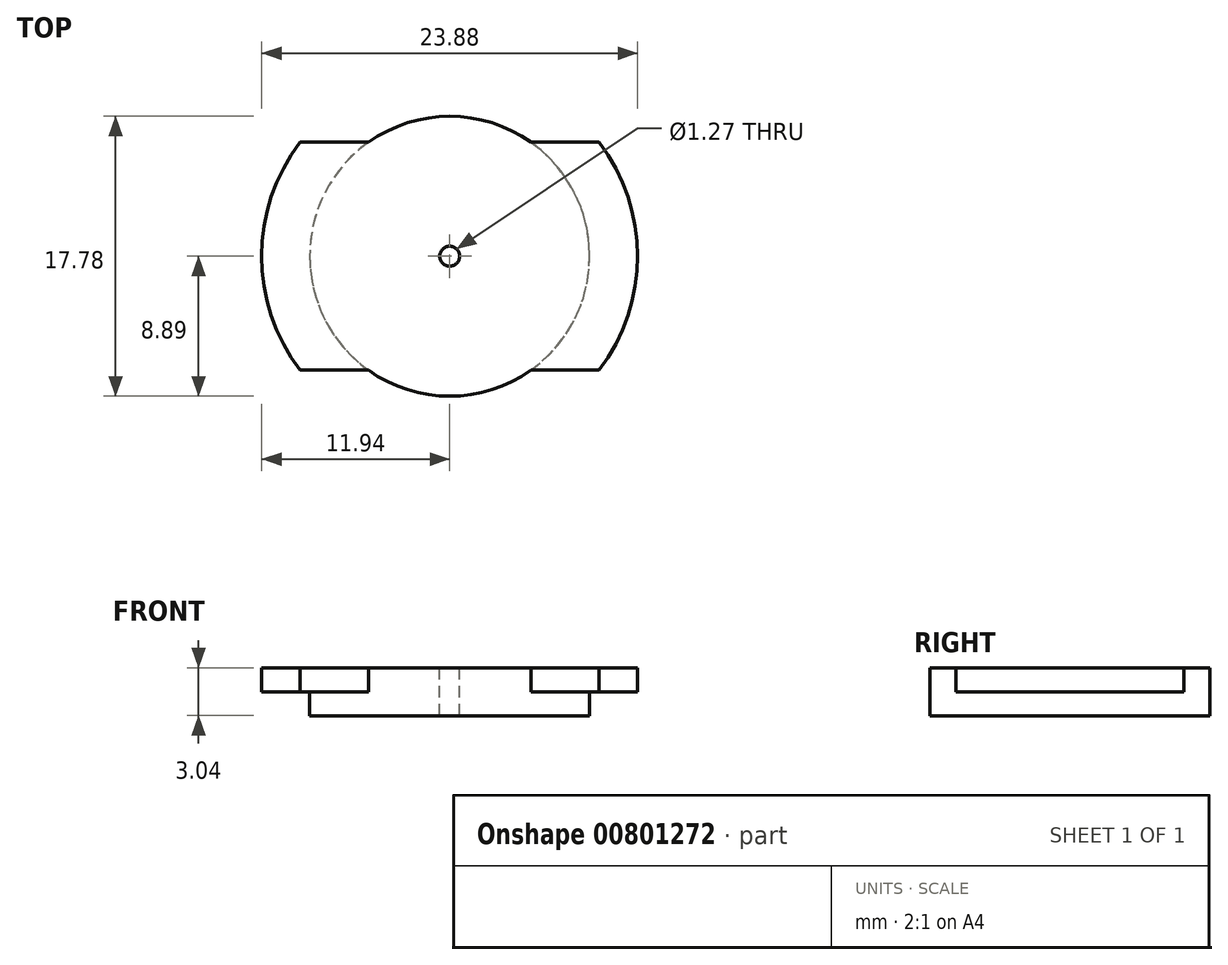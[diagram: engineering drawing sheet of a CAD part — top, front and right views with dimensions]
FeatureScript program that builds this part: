
annotation { "Feature Type Name" : "Feature", "Feature Type Description" : "" }
export const myFeature = defineFeature(function(context is Context, id is Id, definition is map)
    precondition{}
    {
        {
            var Q0;
            Q0=qCreatedBy(makeId("Top.planeOp"),FACE);
            var sketch = newSketch(context, id + "F0", { "sketchPlane" : qUnion([Q0])});
            skCircle(sketch, "E0", {"center": v(0, 0) * mm, "radius": 11.94 * mm});
            skSolve(sketch);
        }
        {
            var Q0;
            Q0=makeQuery(id+"F0.imprint","IMPRINT",FACE,{"disambiguationData":[TD([[makeQuery(id+"F0.imprint","IMPRINT",EDGE,{"derivedFrom":sQuery(id+"F0.wireOp",EDGE,"E0")}),1.0]])]});
            var sketch = newSketch(context, id + "F1", { "sketchPlane" : qUnion([Q0])});
            skLineSegment(sketch, "E1", {"start": v(9.5, 7.24) * mm, "end": v(-9.5, 7.24) * mm});
            skLineSegment(sketch, "E2", {"start": v(9.5, -7.24) * mm, "end": v(-9.5, -7.24) * mm});
            skLineSegment(sketch, "E3", {"start": v(-9.5, 7.24) * mm, "end": v(-9.5, -7.24) * mm, "construction": true});
            skLineSegment(sketch, "E4", {"start": v(9.5, 7.24) * mm, "end": v(9.5, -7.24) * mm, "construction": true});
            skSolve(sketch);
        }
        {
            var Q0;
            Q0 = qSketchRegion(id + "F0", true);
            extrude(context, id + "F2", {"entities" : qUnion([Q0]), "depth" : 1.52 * mm, "offsetDistance" : 25.4 * mm});
        }
        {
            var Q0;
            {var subQ0=sQuery(id+"F1.wireOp",EDGE,"E1");Q0=makeQuery(id+"F1.imprint","IMPRINT",FACE,{"disambiguationData":[TD([[makeQuery(id+"F1.imprint","IMPRINT",EDGE,{"derivedFrom":subQ0}),-1.0]])]});}
            var Q1;
            {var subQ0=sQuery(id+"F1.wireOp",EDGE,"E2");Q1=makeQuery(id+"F1.imprint","IMPRINT",FACE,{"disambiguationData":[TD([[makeQuery(id+"F1.imprint","IMPRINT",EDGE,{"derivedFrom":subQ0}),1.0]])]});}
            extrude(context, id + "F3", {"entities" : qUnion([Q0, Q1]), "operationType" : NewBodyOperationType.REMOVE, "depth" : 2.54 * mm, "offsetDistance" : 25.4 * mm, "hasSecondDirection" : true, "secondDirectionOppositeDirection" : true, "secondDirectionDepth" : 25.4 * mm});
        }
        {
            var Q0;
            Q0=makeQuery(id+"F2.opExtrude","CAP_FACE",FACE,{"disambiguationData":[OSD([sQuery(id+"F0.wireOp",EDGE,"E0")])],"isStart":true});
            var sketch = newSketch(context, id + "F4", { "sketchPlane" : qUnion([Q0])});
            skCircle(sketch, "E5", {"center": v(0, 0) * mm, "radius": 8.9 * mm});
            skSolve(sketch);
        }
        {
            var Q0;
            Q0 = qSketchRegion(id + "F4", true);
            extrude(context, id + "F5", {"entities" : qUnion([Q0]), "operationType" : NewBodyOperationType.ADD, "oppositeDirection" : true, "depth" : 1.52 * mm, "offsetDistance" : 25.4 * mm});
        }
        {
            var Q0;
            Q0=makeQuery(id+"F5.boolean.opBoolean","MERGE",FACE,{"derivedFrom":[makeQuery(id+"F2.opExtrude","CAP_FACE",FACE,{"disambiguationData":[OSD([sQuery(id+"F0.wireOp",EDGE,"E0")])],"isStart":true}),makeQuery(id+"F5.opExtrude","CAP_FACE",FACE,{"disambiguationData":[OSD([sQuery(id+"F4.wireOp",EDGE,"E5")])],"isStart":true})]});
            var sketch = newSketch(context, id + "F6", { "sketchPlane" : qUnion([Q0])});
            skCircle(sketch, "E6", {"center": v(0, 0) * mm, "radius": 8.9 * mm});
            skSolve(sketch);
        }
        {
            var Q0;
            Q0 = qSketchRegion(id + "F6", true);
            extrude(context, id + "F7", {"entities" : qUnion([Q0]), "operationType" : NewBodyOperationType.ADD, "depth" : 1.52 * mm, "offsetDistance" : 25.4 * mm});
        }
        {
            var Q0;
            Q0=makeQuery(id+"F5.boolean.opBoolean","MERGE",FACE,{"derivedFrom":[makeQuery(id+"F2.opExtrude","CAP_FACE",FACE,{"disambiguationData":[OSD([sQuery(id+"F0.wireOp",EDGE,"E0")])],"isStart":false}),makeQuery(id+"F5.opExtrude","CAP_FACE",FACE,{"disambiguationData":[OSD([sQuery(id+"F4.wireOp",EDGE,"E5")])],"isStart":false})]});
            var sketch = newSketch(context, id + "F8", { "sketchPlane" : qUnion([Q0])});
            skCircle(sketch, "E7", {"center": v(0, 0) * mm, "radius": 0.64 * mm});
            skSolve(sketch);
        }
        {
            var Q0;
            Q0 = qSketchRegion(id + "F8", true);
            extrude(context, id + "F9", {"entities" : qUnion([Q0]), "operationType" : NewBodyOperationType.REMOVE, "oppositeDirection" : true, "depth" : 25.4 * mm, "offsetDistance" : 25.4 * mm, "hasSecondDirection" : true, "secondDirectionOppositeDirection" : false, "secondDirectionDepth" : 25.4 * mm});
        }
    });
